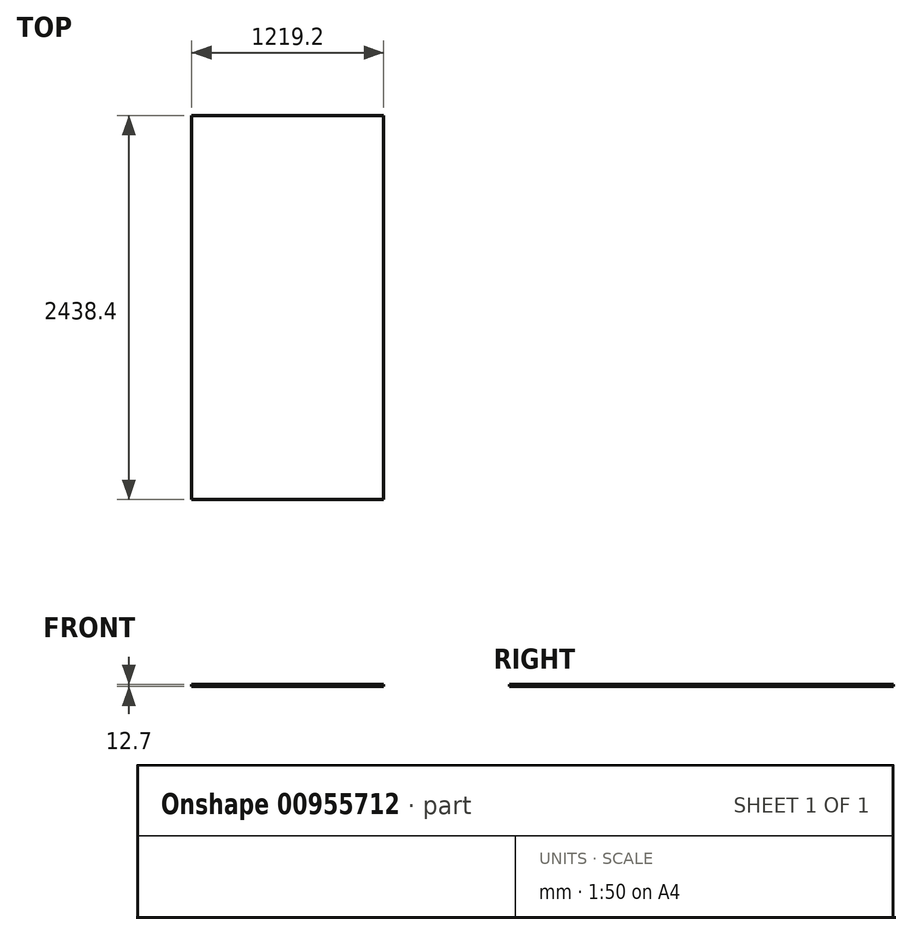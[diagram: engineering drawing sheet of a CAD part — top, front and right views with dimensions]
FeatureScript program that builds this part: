
annotation { "Feature Type Name" : "Feature", "Feature Type Description" : "" }
export const myFeature = defineFeature(function(context is Context, id is Id, definition is map)
    precondition{}
    {
        {
            var Q0;
            Q0=qCreatedBy(makeId("Top.planeOp"),FACE);
            var sketch = newSketch(context, id + "F0", { "sketchPlane" : qUnion([Q0])});
            skLineSegment(sketch, "E0.bottom", {"start": v(609.6, -1219.2) * mm, "end": v(-609.6, -1219.2) * mm});
            skLineSegment(sketch, "E0.top", {"start": v(609.6, 1219.2) * mm, "end": v(-609.6, 1219.2) * mm});
            skLineSegment(sketch, "E0.left", {"start": v(609.6, -1219.2) * mm, "end": v(609.6, 1219.2) * mm});
            skLineSegment(sketch, "E0.right", {"start": v(-609.6, -1219.2) * mm, "end": v(-609.6, 1219.2) * mm});
            skPoint(sketch, "E0.middle", {"position": v(0, 0) * mm});
            skSolve(sketch);
        }
        {
            var Q0;
            Q0=makeQuery(id+"F0.imprint","IMPRINT",FACE,{"disambiguationData":[TD([[makeQuery(id+"F0.imprint","IMPRINT",EDGE,{"derivedFrom":sQuery(id+"F0.wireOp",EDGE,"E0.bottom")}),-1.0]])]});
            extrude(context, id + "F1", {"entities" : qUnion([Q0]), "depth" : 12.7 * mm, "offsetDistance" : 25.4 * mm});
        }
    });
